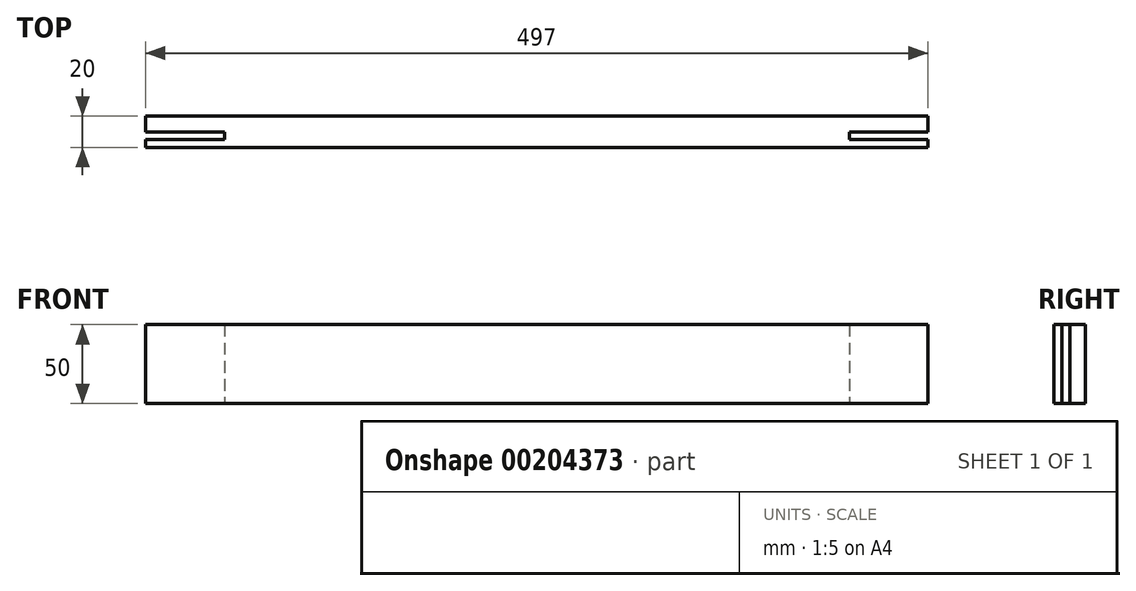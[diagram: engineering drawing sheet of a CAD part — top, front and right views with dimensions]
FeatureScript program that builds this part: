
annotation { "Feature Type Name" : "Feature", "Feature Type Description" : "" }
export const myFeature = defineFeature(function(context is Context, id is Id, definition is map)
    precondition{}
    {
        {
            var Q0;
            Q0=qCreatedBy(makeId("Top.planeOp"),FACE);
            var sketch = newSketch(context, id + "F0", { "sketchPlane" : qUnion([Q0])});
            skLineSegment(sketch, "E0.bottom", {"start": v(0, 0) * mm, "end": v(497, 0) * mm});
            skLineSegment(sketch, "E0.top", {"start": v(0, 20) * mm, "end": v(497, 20) * mm});
            skLineSegment(sketch, "E1", {"start": v(0, 10) * mm, "end": v(50, 10) * mm});
            skLineSegment(sketch, "E2", {"start": v(50, 10) * mm, "end": v(50, 5) * mm});
            skLineSegment(sketch, "E3", {"start": v(50, 5) * mm, "end": v(0, 5) * mm});
            skLineSegment(sketch, "E4", {"start": v(248.5, 0) * mm, "end": v(248.5, -22.06) * mm, "construction": true});
            skLineSegment(sketch, "E5.MirrorCS", {"start": v(497, 10) * mm, "end": v(447, 10) * mm});
            skLineSegment(sketch, "E6.MirrorCS", {"start": v(447, 10) * mm, "end": v(447, 5) * mm});
            skLineSegment(sketch, "E7.MirrorCS", {"start": v(447, 5) * mm, "end": v(497, 5) * mm});
            skLineSegment(sketch, "E8", {"start": v(0, 5) * mm, "end": v(0, 0) * mm});
            skLineSegment(sketch, "E9", {"start": v(0, 20) * mm, "end": v(0, 10) * mm});
            skLineSegment(sketch, "E10", {"start": v(497, 10) * mm, "end": v(497, 20) * mm});
            skLineSegment(sketch, "E11", {"start": v(497, 5) * mm, "end": v(497, 0) * mm});
            skSolve(sketch);
        }
        {
            var Q0;
            Q0=qSketchRegion(id+"F0",true);
            extrude(context, id + "F1", {"entities" : qUnion([Q0]), "depth" : 50 * mm});
        }
    });
